# Revit family: TopVent_MH
name_source: partatom
category: Mechanical Equipment
revit_build: Autodesk Revit MEP 2015 (Build: 20160512_0715(x64)
units: mm (PartAtom-declared; Revit-internal decimal feet)

## types (6) — shared parameters
COBIE Extract air temperature max. = 50°C
COBIE Frequency = 50 Hz
COBIE Permitted voltage tolerance = +/-5%
COBIE Pressure of the heating medium max. = 800 kPa
COBIE Protection rating = IP 54
COBIE Series fuse = 13A
COBIE Supply air temperature max. = 60°C
COBIE Supply voltage = 3x400 V AC
COBIE Temperature of the heating medium max. = 90°C
E = 594 mm  [stored 1.94882 ft]
E/2 = 297 mm  [stored 0.974409 ft]
Extract air temperature max. = 50°C
Frequency = 50 Hz
Permitted voltage tolerance = +/-5%
Pressure of the heating medium max. = 800 kPa
Protection rating = IP 54
Series fuse = 13A
Supply air temperature max. = 60°C
Supply voltage = 3x400 V AC
Temperature of the heating medium max. = 90°C

## per-type parameters (varying)
- MH-6-A: A=900 mm  [stored 2.95276 ft]; COBIE Connected load=1.5 kW; COBIE Current consumption max.=2.9A; COBIE Effective electric power input=0.90 kW; COBIE Floor area covered=537.0; COBIE Heat output -5/-15 °C (60/40 °C)=19.1/19.7 kW; COBIE Heat output -5/-15 °C (80/60 °C)=33.1/33.8 kW; COBIE Maximum mounting height -5/-15 °C (60/40 °C)=18.8/19.5 m; COBIE Maximum mounting height -5/-15 °C (80/60 °C)=14.4/14.7 m; COBIE Nominal air flow rate=6000.0; COBIE Octave sound power level - 1000 Hz=76 dB; COBIE Octave sound power level - 125 Hz=61 dB; COBIE Octave sound power level - 2000 Hz=73 dB; COBIE Octave sound power level - 250 Hz=67 dB; COBIE Octave sound power level - 4000 Hz=67 dB; COBIE Octave sound power level - 500 Hz=72 dB; COBIE Octave sound power level - 63 Hz=57 dB; COBIE Octave sound power level - 8000 Hz=59 dB; COBIE Sound pressure level (at a distance of 5 m)=58 dB(A); COBIE Static efficiency of the fans=48.5%; COBIE Supply air temperature -5/-15 °C (60/40 °C)=27.0/26.3 °C; COBIE Supply air temperature -5/-15 °C (80/60 °C)=33.9/33.2 °C; COBIE Total sound power level=80 dB(A); COBIE Water content of heating coil=4.6 l; COBIE Water pressure drop -5/-15 °C (60/40 °C)=2/3 kPa; COBIE Water pressure drop -5/-15 °C (80/60 °C)=7/8 kPa; COBIE Water quantity -5/-15 °C (60/40 °C)=820/848 l/h; COBIE Water quantity -5/-15 °C (80/60 °C)=1424/1451 l/h; COBIE Weight=165 kg; Connected load=1.5 kW; Current consumption max.=2.9A; Effective electric power input=0.90 kW; F=758 mm  [stored 2.48688 ft]; Floor area covered=537 m²; G=1077 mm  [stored 3.53346 ft]; H=999 mm  [stored 3.27756 ft]; Heat output -5/-15 °C (60/40 °C)=19.1/19.7 kW; Heat output -5/-15 °C (80/60 °C)=33.1/33.8 kW; I=760 mm  [stored 2.49344 ft]; J=32 mm; K=1089 mm  [stored 3.57283 ft]; Maximum mounting height -5/-15 °C (60/40 °C)=18.8/19.5 m; Maximum mounting height -5/-15 °C (80/60 °C)=14.4/14.7 m; Nominal air flow rate=6000 m³/h; O=420 mm  [stored 1.37795 ft]; Octave sound power level - 1000 Hz=76 dB; Octave sound power level - 125 Hz=61 dB; Octave sound power level - 2000 Hz=73 dB; Octave sound power level - 250 Hz=67 dB; Octave sound power level - 4000 Hz=67 dB; Octave sound power level - 500 Hz=72 dB; Octave sound power level - 63 Hz=57 dB; Octave sound power level - 8000 Hz=59 dB; P=850 mm  [stored 2.78871 ft]; R=1660 mm  [stored 5.44619 ft]; Sound pressure level (at a distance of 5 m)=58 dB(A); Static efficiency of the fans=48.5%; Supply air temperature -5/-15 °C (60/40 °C)=27.0/26.3 °C; Supply air temperature -5/-15 °C (80/60 °C)=33.9/33.2 °C; Total sound power level=80 dB(A); Water content of heating coil=4.6 l; Water pressure drop -5/-15 °C (60/40 °C)=2/3 kPa; Water pressure drop -5/-15 °C (80/60 °C)=7/8 kPa; Water quantity -5/-15 °C (60/40 °C)=820/848 l/h; Water quantity -5/-15 °C (80/60 °C)=1424/1451 l/h; Weight=165 kg
- MH-6-B: A=900 mm  [stored 2.95276 ft]; COBIE Connected load=1.5 kW; COBIE Current consumption max.=2.9A; COBIE Effective electric power input=1.05 kW; COBIE Floor area covered=537.0; COBIE Heat output -5/-15 °C (60/40 °C)=27.4/28.3 kW; COBIE Heat output -5/-15 °C (80/60 °C)=47.5/48.4 kW; COBIE Maximum mounting height -5/-15 °C (60/40 °C)=15.7/16.1 m; COBIE Maximum mounting height -5/-15 °C (80/60 °C)=12.1/12.2 m; COBIE Nominal air flow rate=6000.0; COBIE Octave sound power level - 1000 Hz=76 dB; COBIE Octave sound power level - 125 Hz=61 dB; COBIE Octave sound power level - 2000 Hz=73 dB; COBIE Octave sound power level - 250 Hz=67 dB; COBIE Octave sound power level - 4000 Hz=67 dB; COBIE Octave sound power level - 500 Hz=72 dB; COBIE Octave sound power level - 63 Hz=57 dB; COBIE Octave sound power level - 8000 Hz=59 dB; COBIE Sound pressure level (at a distance of 5 m)=58 dB(A); COBIE Static efficiency of the fans=48.5%; COBIE Supply air temperature -5/-15 °C (60/40 °C)=31.1/30.5 °C; COBIE Supply air temperature -5/-15 °C (80/60 °C)=41.0/40.5 °C; COBIE Total sound power level=80 dB(A); COBIE Water content of heating coil=4.6 l; COBIE Water pressure drop -5/-15 °C (60/40 °C)=4/5 kPa; COBIE Water pressure drop -5/-15 °C (80/60 °C)=13/14 kPa; COBIE Water quantity -5/-15 °C (60/40 °C)=1177/1216 l/h; COBIE Water quantity -5/-15 °C (80/60 °C)=2040/2079 l/h; COBIE Weight=165 kg; Connected load=1.5 kW; Current consumption max.=2.9A; Effective electric power input=1.05 kW; F=758 mm  [stored 2.48688 ft]; Floor area covered=537 m²; G=1077 mm  [stored 3.53346 ft]; H=999 mm  [stored 3.27756 ft]; Heat output -5/-15 °C (60/40 °C)=27.4/28.3 kW; Heat output -5/-15 °C (80/60 °C)=47.5/48.4 kW; I=760 mm  [stored 2.49344 ft]; J=32 mm; K=1089 mm  [stored 3.57283 ft]; Maximum mounting height -5/-15 °C (60/40 °C)=15.7/16.1 m; Maximum mounting height -5/-15 °C (80/60 °C)=12.1/12.2 m; Nominal air flow rate=6000 m³/h; O=420 mm  [stored 1.37795 ft]; Octave sound power level - 1000 Hz=76 dB; Octave sound power level - 125 Hz=61 dB; Octave sound power level - 2000 Hz=73 dB; Octave sound power level - 250 Hz=67 dB; Octave sound power level - 4000 Hz=67 dB; Octave sound power level - 500 Hz=72 dB; Octave sound power level - 63 Hz=57 dB; Octave sound power level - 8000 Hz=59 dB; P=850 mm  [stored 2.78871 ft]; R=1660 mm  [stored 5.44619 ft]; Sound pressure level (at a distance of 5 m)=58 dB(A); Static efficiency of the fans=48.5%; Supply air temperature -5/-15 °C (60/40 °C)=31.1/30.5 °C; Supply air temperature -5/-15 °C (80/60 °C)=41.0/40.5 °C; Total sound power level=80 dB(A); Water content of heating coil=4.6 l; Water pressure drop -5/-15 °C (60/40 °C)=4/5 kPa; Water pressure drop -5/-15 °C (80/60 °C)=13/14 kPa; Water quantity -5/-15 °C (60/40 °C)=1177/1216 l/h; Water quantity -5/-15 °C (80/60 °C)=2040/2079 l/h; Weight=165 kg
- MH-6-C: A=900 mm  [stored 2.95276 ft]; COBIE Connected load=1.5 kW; COBIE Current consumption max.=2.9A; COBIE Effective electric power input=1.29 kW; COBIE Floor area covered=537.0; COBIE Heat output -5/-15 °C (60/40 °C)=45.7/47.2 kW; COBIE Heat output -5/-15 °C (80/60 °C)=76.8/78.2 kW; COBIE Maximum mounting height -5/-15 °C (60/40 °C)=12.3/12.4 m; COBIE Maximum mounting height -5/-15 °C (80/60 °C)=9.7/9.7 m; COBIE Nominal air flow rate=6000.0; COBIE Octave sound power level - 1000 Hz=76 dB; COBIE Octave sound power level - 125 Hz=61 dB; COBIE Octave sound power level - 2000 Hz=73 dB; COBIE Octave sound power level - 250 Hz=67 dB; COBIE Octave sound power level - 4000 Hz=67 dB; COBIE Octave sound power level - 500 Hz=72 dB; COBIE Octave sound power level - 63 Hz=57 dB; COBIE Octave sound power level - 8000 Hz=59 dB; COBIE Sound pressure level (at a distance of 5 m)=58 dB(A); COBIE Static efficiency of the fans=48.5%; COBIE Supply air temperature -5/-15 °C (60/40 °C)=40.1/39.9 °C; COBIE Supply air temperature -5/-15 °C (80/60 °C)=55.5/55.2 °C; COBIE Total sound power level=80 dB(A); COBIE Water content of heating coil=7.9 l; COBIE Water pressure drop -5/-15 °C (60/40 °C)=7/7 kPa; COBIE Water pressure drop -5/-15 °C (80/60 °C)=18/19 kPa; COBIE Water quantity -5/-15 °C (60/40 °C)=1965/2026 l/h; COBIE Water quantity -5/-15 °C (80/60 °C)=3297/3358 l/h; COBIE Weight=172 kg; Connected load=1.5 kW; Current consumption max.=2.9A; Effective electric power input=1.29 kW; F=758 mm  [stored 2.48688 ft]; Floor area covered=537 m²; G=1077 mm  [stored 3.53346 ft]; H=999 mm  [stored 3.27756 ft]; Heat output -5/-15 °C (60/40 °C)=45.7/47.2 kW; Heat output -5/-15 °C (80/60 °C)=76.8/78.2 kW; I=760 mm  [stored 2.49344 ft]; J=32 mm; K=1089 mm  [stored 3.57283 ft]; Maximum mounting height -5/-15 °C (60/40 °C)=12.3/12.4 m; Maximum mounting height -5/-15 °C (80/60 °C)=9.7/9.7 m; Nominal air flow rate=6000 m³/h; O=420 mm  [stored 1.37795 ft]; Octave sound power level - 1000 Hz=76 dB; Octave sound power level - 125 Hz=61 dB; Octave sound power level - 2000 Hz=73 dB; Octave sound power level - 250 Hz=67 dB; Octave sound power level - 4000 Hz=67 dB; Octave sound power level - 500 Hz=72 dB; Octave sound power level - 63 Hz=57 dB; Octave sound power level - 8000 Hz=59 dB; P=850 mm  [stored 2.78871 ft]; R=1660 mm  [stored 5.44619 ft]; Sound pressure level (at a distance of 5 m)=58 dB(A); Static efficiency of the fans=48.5%; Supply air temperature -5/-15 °C (60/40 °C)=40.1/39.9 °C; Supply air temperature -5/-15 °C (80/60 °C)=55.5/55.2 °C; Total sound power level=80 dB(A); Water content of heating coil=7.9 l; Water pressure drop -5/-15 °C (60/40 °C)=7/7 kPa; Water pressure drop -5/-15 °C (80/60 °C)=18/19 kPa; Water quantity -5/-15 °C (60/40 °C)=1965/2026 l/h; Water quantity -5/-15 °C (80/60 °C)=3297/3358 l/h; Weight=172 kg
- MH-9-A: A=1100 mm; COBIE Connected load=2.1 kW; COBIE Current consumption max.=4.0A; COBIE Effective electric power input=1.37 kW; COBIE Floor area covered=946.0; COBIE Heat output -5/-15 °C (60/40 °C)=32.3/33.4 kW; COBIE Heat output -5/-15 °C (80/60 °C)=56.1/57.1 kW; COBIE Maximum mounting height -5/-15 °C (60/40 °C)=18.8/19.4 m; COBIE Maximum mounting height -5/-15 °C (80/60 °C)=14.4/14.6 m; COBIE Nominal air flow rate=9000.0; COBIE Octave sound power level - 1000 Hz=77 dB; COBIE Octave sound power level - 125 Hz=66 dB; COBIE Octave sound power level - 2000 Hz=76 dB; COBIE Octave sound power level - 250 Hz=71 dB; COBIE Octave sound power level - 4000 Hz=71 dB; COBIE Octave sound power level - 500 Hz=74 dB; COBIE Octave sound power level - 63 Hz=62 dB; COBIE Octave sound power level - 8000 Hz=64 dB; COBIE Sound pressure level (at a distance of 5 m)=60 dB(A); COBIE Static efficiency of the fans=43.0%; COBIE Supply air temperature -5/-15 °C (60/40 °C)=28.2/27.5 °C; COBIE Supply air temperature -5/-15 °C (80/60 °C)=36.0/35.4 °C; COBIE Total sound power level=82 dB(A); COBIE Water content of heating coil=7.4 l; COBIE Water pressure drop -5/-15 °C (60/40 °C)=3/3 kPa; COBIE Water pressure drop -5/-15 °C (80/60 °C)=8/8 kPa; COBIE Water quantity -5/-15 °C (60/40 °C)=1387/1433 l/h; COBIE Water quantity -5/-15 °C (80/60 °C)=2409/2455 l/h; COBIE Weight=217 kg; Connected load=2.1 kW; Current consumption max.=4.0A; Effective electric power input=1.37 kW; F=882 mm  [stored 2.8937 ft]; Floor area covered=946 m²; G=1127 mm  [stored 3.69751 ft]; H=1049 mm  [stored 3.4416 ft]; Heat output -5/-15 °C (60/40 °C)=32.3/33.4 kW; Heat output -5/-15 °C (80/60 °C)=56.1/57.1 kW; I=935 mm; J=38 mm; K=1289 mm; Maximum mounting height -5/-15 °C (60/40 °C)=18.8/19.4 m; Maximum mounting height -5/-15 °C (80/60 °C)=14.4/14.6 m; Nominal air flow rate=9000 m³/h; O=500 mm  [stored 1.64042 ft]; Octave sound power level - 1000 Hz=77 dB; Octave sound power level - 125 Hz=66 dB; Octave sound power level - 2000 Hz=76 dB; Octave sound power level - 250 Hz=71 dB; Octave sound power level - 4000 Hz=71 dB; Octave sound power level - 500 Hz=74 dB; Octave sound power level - 63 Hz=62 dB; Octave sound power level - 8000 Hz=64 dB; P=1050 mm; R=1810 mm  [stored 5.93832 ft]; Sound pressure level (at a distance of 5 m)=60 dB(A); Static efficiency of the fans=43.0%; Supply air temperature -5/-15 °C (60/40 °C)=28.2/27.5 °C; Supply air temperature -5/-15 °C (80/60 °C)=36.0/35.4 °C; Total sound power level=82 dB(A); Water content of heating coil=7.4 l; Water pressure drop -5/-15 °C (60/40 °C)=3/3 kPa; Water pressure drop -5/-15 °C (80/60 °C)=8/8 kPa; Water quantity -5/-15 °C (60/40 °C)=1387/1433 l/h; Water quantity -5/-15 °C (80/60 °C)=2409/2455 l/h; Weight=217 kg
- MH-9-B: A=1100 mm; COBIE Connected load=2.1 kW; COBIE Current consumption max.=4.0A; COBIE Effective electric power input=1.49 kW; COBIE Floor area covered=946.0; COBIE Heat output -5/-15 °C (60/40 °C)=41.3/42.7 kW; COBIE Heat output -5/-15 °C (80/60 °C)=71.9/73.3 kW; COBIE Maximum mounting height -5/-15 °C (60/40 °C)=16.7/17.0 m; COBIE Maximum mounting height -5/-15 °C (80/60 °C)=12.8/12.9 m; COBIE Nominal air flow rate=9000.0; COBIE Octave sound power level - 1000 Hz=77 dB; COBIE Octave sound power level - 125 Hz=66 dB; COBIE Octave sound power level - 2000 Hz=76 dB; COBIE Octave sound power level - 250 Hz=71 dB; COBIE Octave sound power level - 4000 Hz=71 dB; COBIE Octave sound power level - 500 Hz=74 dB; COBIE Octave sound power level - 63 Hz=62 dB; COBIE Octave sound power level - 8000 Hz=64 dB; COBIE Sound pressure level (at a distance of 5 m)=60 dB(A); COBIE Static efficiency of the fans=43.0%; COBIE Supply air temperature -5/-15 °C (60/40 °C)=31.1/30.6 °C; COBIE Supply air temperature -5/-15 °C (80/60 °C)=41.2/40.7 °C; COBIE Total sound power level=82 dB(A); COBIE Water content of heating coil=7.4 l; COBIE Water pressure drop -5/-15 °C (60/40 °C)=4/4 kPa; COBIE Water pressure drop -5/-15 °C (80/60 °C)=12/13 kPa; COBIE Water quantity -5/-15 °C (60/40 °C)=1775/1834 l/h; COBIE Water quantity -5/-15 °C (80/60 °C)=3090/3149 l/h; COBIE Weight=217 kg; Connected load=2.1 kW; Current consumption max.=4.0A; Effective electric power input=1.49 kW; F=882 mm  [stored 2.8937 ft]; Floor area covered=946 m²; G=1127 mm  [stored 3.69751 ft]; H=1049 mm  [stored 3.4416 ft]; Heat output -5/-15 °C (60/40 °C)=41.3/42.7 kW; Heat output -5/-15 °C (80/60 °C)=71.9/73.3 kW; I=935 mm; J=38 mm; K=1289 mm; Maximum mounting height -5/-15 °C (60/40 °C)=16.7/17.0 m; Maximum mounting height -5/-15 °C (80/60 °C)=12.8/12.9 m; Nominal air flow rate=9000 m³/h; O=500 mm  [stored 1.64042 ft]; Octave sound power level - 1000 Hz=77 dB; Octave sound power level - 125 Hz=66 dB; Octave sound power level - 2000 Hz=76 dB; Octave sound power level - 250 Hz=71 dB; Octave sound power level - 4000 Hz=71 dB; Octave sound power level - 500 Hz=74 dB; Octave sound power level - 63 Hz=62 dB; Octave sound power level - 8000 Hz=64 dB; P=1050 mm; R=1810 mm  [stored 5.93832 ft]; Sound pressure level (at a distance of 5 m)=60 dB(A); Static efficiency of the fans=43.0%; Supply air temperature -5/-15 °C (60/40 °C)=31.1/30.6 °C; Supply air temperature -5/-15 °C (80/60 °C)=41.2/40.7 °C; Total sound power level=82 dB(A); Water content of heating coil=7.4 l; Water pressure drop -5/-15 °C (60/40 °C)=4/4 kPa; Water pressure drop -5/-15 °C (80/60 °C)=12/13 kPa; Water quantity -5/-15 °C (60/40 °C)=1775/1834 l/h; Water quantity -5/-15 °C (80/60 °C)=3090/3149 l/h; Weight=217 kg
- MH-9-C: A=1100 mm; COBIE Connected load=2.1 kW; COBIE Current consumption max.=4.0A; COBIE Effective electric power input=1.91 kW; COBIE Floor area covered=946.0; COBIE Heat output -5/-15 °C (60/40 °C)=71.0/73.2 kW; COBIE Heat output -5/-15 °C (80/60 °C)=119.0/121.2 kW; COBIE Maximum mounting height -5/-15 °C (60/40 °C)=12.9/12.9 m; COBIE Maximum mounting height -5/-15 °C (80/60 °C)=10.1/10.1 m; COBIE Nominal air flow rate=9000.0; COBIE Octave sound power level - 1000 Hz=77 dB; COBIE Octave sound power level - 125 Hz=66 dB; COBIE Octave sound power level - 2000 Hz=76 dB; COBIE Octave sound power level - 250 Hz=71 dB; COBIE Octave sound power level - 4000 Hz=71 dB; COBIE Octave sound power level - 500 Hz=74 dB; COBIE Octave sound power level - 63 Hz=62 dB; COBIE Octave sound power level - 8000 Hz=64 dB; COBIE Sound pressure level (at a distance of 5 m)=60 dB(A); COBIE Static efficiency of the fans=43.0%; COBIE Supply air temperature -5/-15 °C (60/40 °C)=40.9/40.7 °C; COBIE Supply air temperature -5/-15 °C (80/60 °C)=56.8/56.5 °C; COBIE Total sound power level=82 dB(A); COBIE Water content of heating coil=12.4 l; COBIE Water pressure drop -5/-15 °C (60/40 °C)=7/7 kPa; COBIE Water pressure drop -5/-15 °C (80/60 °C)=18/19 kPa; COBIE Water quantity -5/-15 °C (60/40 °C)=3050/3145 l/h; COBIE Water quantity -5/-15 °C (80/60 °C)=5113/5208 l/h; COBIE Weight=228 kg; Connected load=2.1 kW; Current consumption max.=4.0A; Effective electric power input=1.91 kW; F=882 mm  [stored 2.8937 ft]; Floor area covered=946 m²; G=1127 mm  [stored 3.69751 ft]; H=1049 mm  [stored 3.4416 ft]; Heat output -5/-15 °C (60/40 °C)=71.0/73.2 kW; Heat output -5/-15 °C (80/60 °C)=119.0/121.2 kW; I=935 mm; J=38 mm; K=1289 mm; Maximum mounting height -5/-15 °C (60/40 °C)=12.9/12.9 m; Maximum mounting height -5/-15 °C (80/60 °C)=10.1/10.1 m; Nominal air flow rate=9000 m³/h; O=500 mm  [stored 1.64042 ft]; Octave sound power level - 1000 Hz=77 dB; Octave sound power level - 125 Hz=66 dB; Octave sound power level - 2000 Hz=76 dB; Octave sound power level - 250 Hz=71 dB; Octave sound power level - 4000 Hz=71 dB; Octave sound power level - 500 Hz=74 dB; Octave sound power level - 63 Hz=62 dB; Octave sound power level - 8000 Hz=64 dB; P=1050 mm; R=1810 mm  [stored 5.93832 ft]; Sound pressure level (at a distance of 5 m)=60 dB(A); Static efficiency of the fans=43.0%; Supply air temperature -5/-15 °C (60/40 °C)=40.9/40.7 °C; Supply air temperature -5/-15 °C (80/60 °C)=56.8/56.5 °C; Total sound power level=82 dB(A); Water content of heating coil=12.4 l; Water pressure drop -5/-15 °C (60/40 °C)=7/7 kPa; Water pressure drop -5/-15 °C (80/60 °C)=18/19 kPa; Water quantity -5/-15 °C (60/40 °C)=3050/3145 l/h; Water quantity -5/-15 °C (80/60 °C)=5113/5208 l/h; Weight=228 kg

note: [stored X ft] marks values corroborated as IEEE doubles in the binary element streams (Revit-internal decimal feet)

## geometry (parser evidence)
native form markers: Sweep x7
no freeform markers — native parametric forms only
